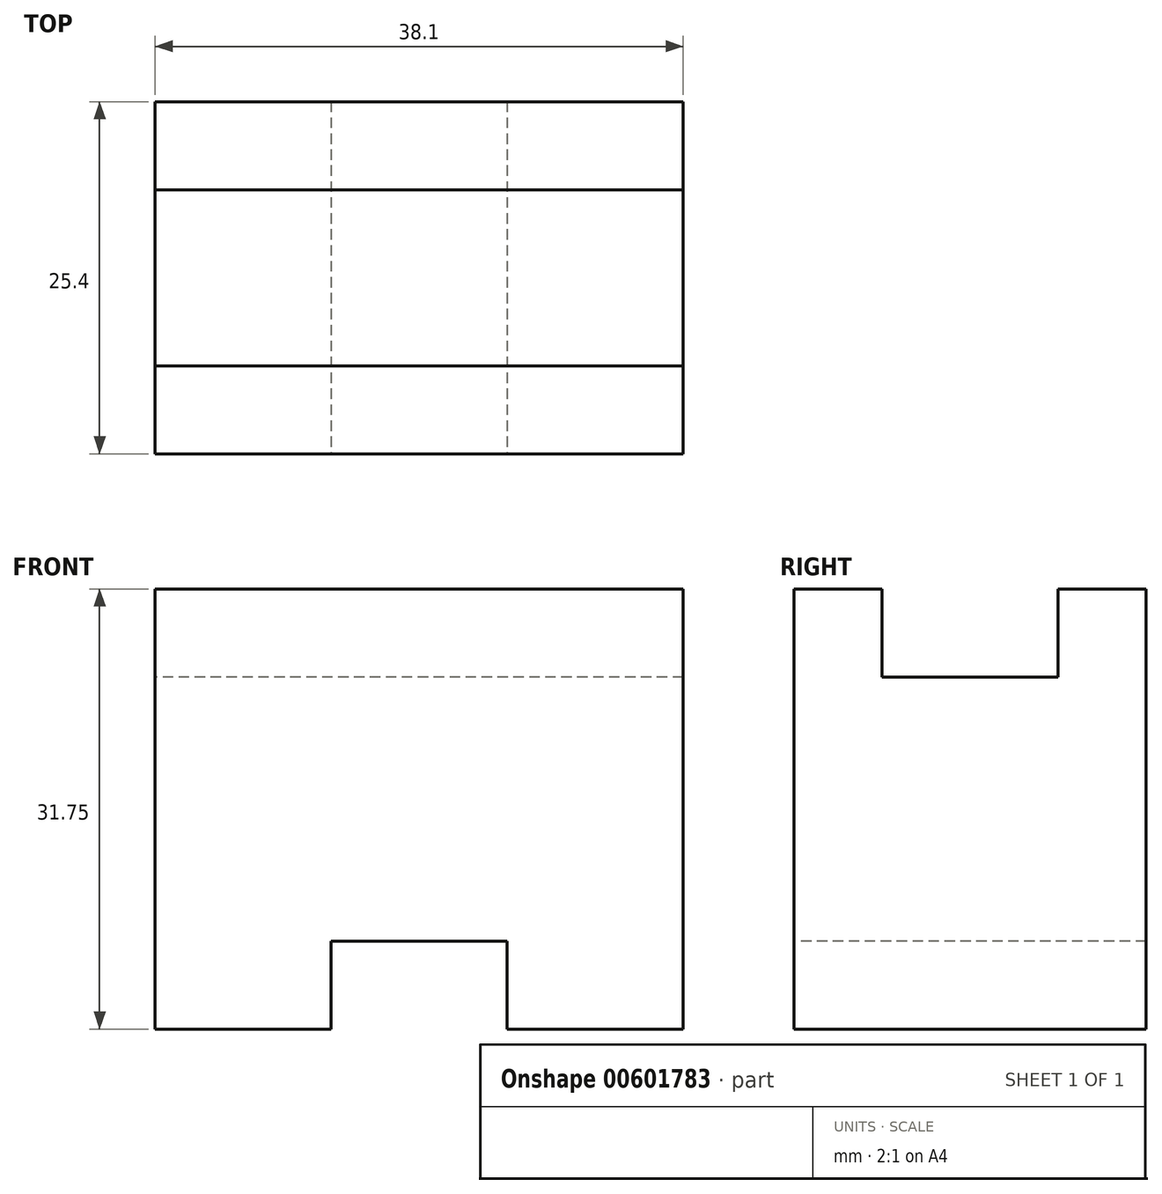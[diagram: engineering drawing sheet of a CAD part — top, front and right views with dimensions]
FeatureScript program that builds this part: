
annotation { "Feature Type Name" : "Feature", "Feature Type Description" : "" }
export const myFeature = defineFeature(function(context is Context, id is Id, definition is map)
    precondition{}
    {
        {
            var Q0;
            Q0=qCreatedBy(makeId("Right.planeOp"),FACE);
            var sketch = newSketch(context, id + "F0", { "sketchPlane" : qUnion([Q0])});
            skLineSegment(sketch, "E0", {"start": v(0, 0) * mm, "end": v(25.4, 0) * mm});
            skLineSegment(sketch, "E1", {"start": v(0, 0) * mm, "end": v(0, 31.75) * mm});
            skLineSegment(sketch, "E2", {"start": v(25.4, 0) * mm, "end": v(25.4, 31.75) * mm});
            skLineSegment(sketch, "E3", {"start": v(0, 31.75) * mm, "end": v(6.35, 31.75) * mm});
            skLineSegment(sketch, "E4", {"start": v(25.4, 31.75) * mm, "end": v(19.05, 31.75) * mm});
            skLineSegment(sketch, "E5", {"start": v(6.35, 31.75) * mm, "end": v(6.35, 25.4) * mm});
            skLineSegment(sketch, "E6", {"start": v(19.05, 31.75) * mm, "end": v(19.05, 25.4) * mm});
            skLineSegment(sketch, "E7", {"start": v(6.35, 25.4) * mm, "end": v(19.05, 25.4) * mm});
            skSolve(sketch);
        }
        {
            var Q0;
            Q0=makeQuery(id+"F0.imprint","IMPRINT",FACE,{"disambiguationData":[TD([[makeQuery(id+"F0.imprint","IMPRINT",EDGE,{"derivedFrom":sQuery(id+"F0.wireOp",EDGE,"E0")}),1.0]])]});
            extrude(context, id + "F1", {"entities" : qUnion([Q0]), "depth" : 38.1 * mm, "offsetDistance" : 25.4 * mm});
        }
        {
            var Q0;
            Q0=makeQuery(id+"F1.opExtrude","SWEPT_FACE",FACE,{"disambiguationData":[OSD([sQuery(id+"F0.wireOp",EDGE,"E1")])]});
            var sketch = newSketch(context, id + "F2", { "sketchPlane" : qUnion([Q0])});
            skLineSegment(sketch, "E8", {"start": v(0, 0) * mm, "end": v(12.7, 0) * mm});
            skLineSegment(sketch, "E9", {"start": v(12.7, 0) * mm, "end": v(12.7, 6.35) * mm});
            skLineSegment(sketch, "E10", {"start": v(12.7, 6.35) * mm, "end": v(25.4, 6.35) * mm});
            skLineSegment(sketch, "E11", {"start": v(25.4, 6.35) * mm, "end": v(25.4, 0) * mm});
            skSolve(sketch);
        }
        {
            var Q0;
            Q0 = qSketchRegion(id + "F2", true);
            var Q1;
            {var subQ0=sQuery(id+"F2.wireOp",EDGE,"E9");Q1=makeQuery(id+"F2.imprint","IMPRINT",FACE,{"disambiguationData":[TD([[makeQuery(id+"F2.imprint","IMPRINT",EDGE,{"derivedFrom":subQ0}),-1.0]])]});}
            extrude(context, id + "F3", {"entities" : qUnion([Q0, Q1]), "operationType" : NewBodyOperationType.REMOVE, "oppositeDirection" : true, "depth" : 25.4 * mm, "offsetDistance" : 25.4 * mm});
        }
    });
